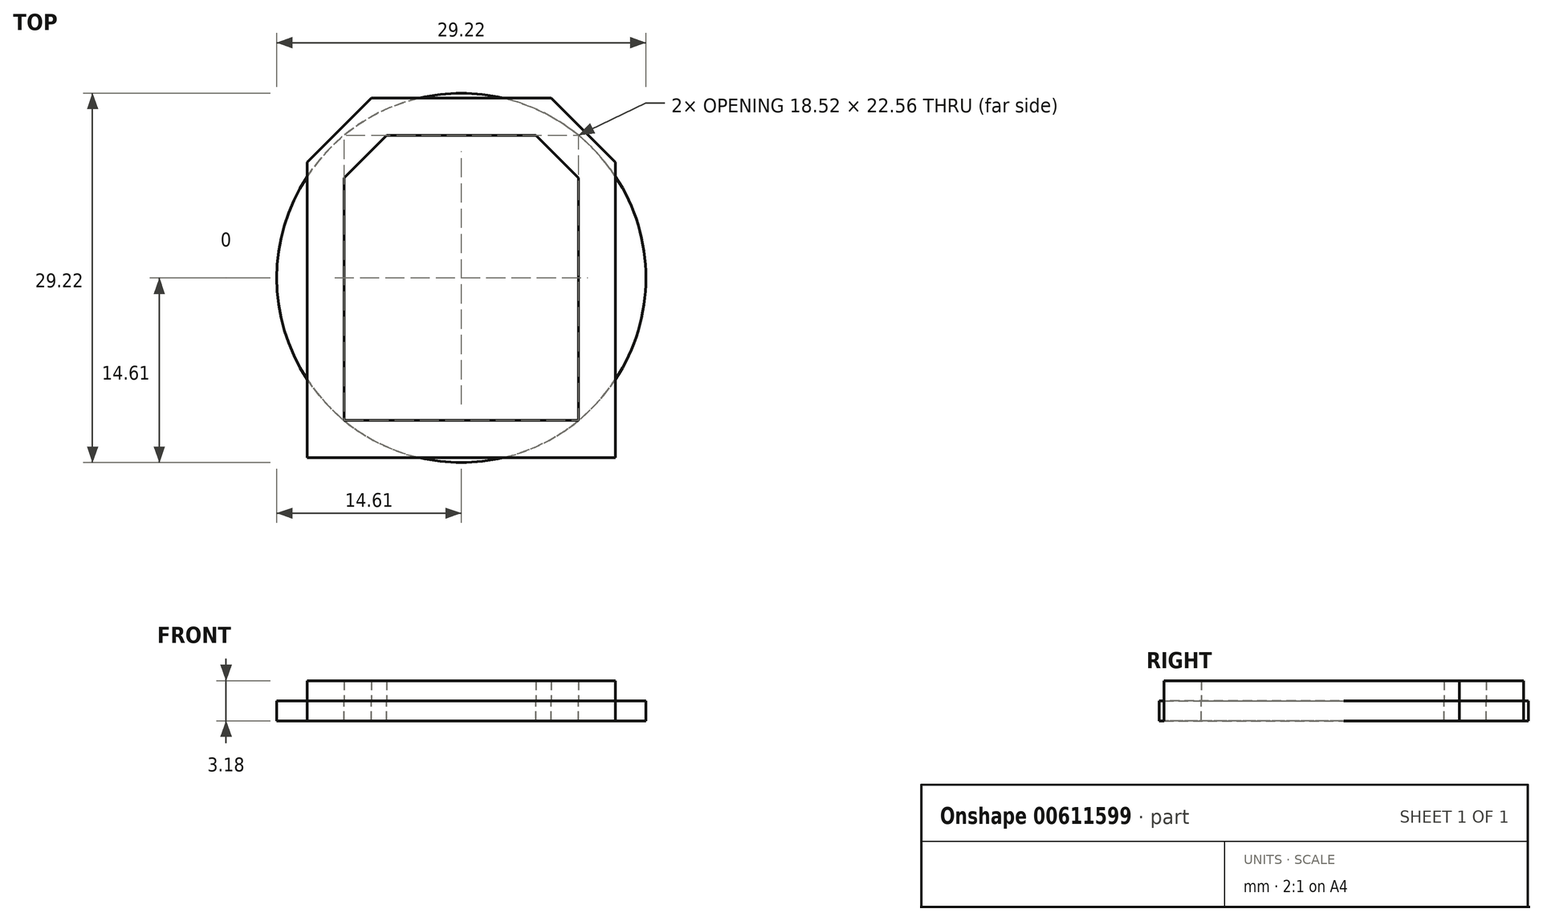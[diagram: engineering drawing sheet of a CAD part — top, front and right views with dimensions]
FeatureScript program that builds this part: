
annotation { "Feature Type Name" : "Feature", "Feature Type Description" : "" }
export const myFeature = defineFeature(function(context is Context, id is Id, definition is map)
    precondition{}
    {
        {
            var Q0;
            Q0=qCreatedBy(makeId("Top.planeOp"),FACE);
            var sketch = newSketch(context, id + "F0", { "sketchPlane" : qUnion([Q0])});
            skLineSegment(sketch, "E0.bottom", {"start": v(12.2, -14.22) * mm, "end": v(-12.2, -14.22) * mm});
            skLineSegment(sketch, "E0.top", {"start": v(7.12, 14.22) * mm, "end": v(-7.12, 14.22) * mm});
            skLineSegment(sketch, "E0.left", {"start": v(12.2, -14.22) * mm, "end": v(12.2, 9.14) * mm});
            skLineSegment(sketch, "E0.right", {"start": v(-12.2, -14.22) * mm, "end": v(-12.2, 9.14) * mm});
            skPoint(sketch, "E0.middle", {"position": v(0, 0) * mm});
            skLineSegment(sketch, "E1", {"start": v(12.2, 9.14) * mm, "end": v(7.12, 14.22) * mm});
            skLineSegment(sketch, "E2.MirrorCS", {"start": v(-12.2, 9.14) * mm, "end": v(-7.12, 14.22) * mm});
            skPoint(sketch, "E3.orphan", {"position": v(-12.2, 14.22) * mm});
            skPoint(sketch, "E4.orphan", {"position": v(12.2, 14.22) * mm});
            skLineSegment(sketch, "E5.0", {"start": v(-9.26, -11.28) * mm, "end": v(-9.26, 7.92) * mm});
            skLineSegment(sketch, "E5.1", {"start": v(5.9, 11.28) * mm, "end": v(-5.9, 11.28) * mm});
            skLineSegment(sketch, "E5.2", {"start": v(9.26, 7.92) * mm, "end": v(5.9, 11.28) * mm});
            skLineSegment(sketch, "E5.3", {"start": v(-9.26, 7.92) * mm, "end": v(-5.9, 11.28) * mm});
            skLineSegment(sketch, "E5.4", {"start": v(9.26, -11.28) * mm, "end": v(9.26, 7.92) * mm});
            skLineSegment(sketch, "E5.5", {"start": v(9.26, -11.28) * mm, "end": v(-9.26, -11.28) * mm});
            skSolve(sketch);
        }
        {
            var Q0;
            Q0=makeQuery(id+"F0.imprint","IMPRINT",FACE,{"disambiguationData":[TD([[makeQuery(id+"F0.imprint","IMPRINT",EDGE,{"derivedFrom":sQuery(id+"F0.wireOp",EDGE,"E0.bottom")}),-1.0]])]});
            extrude(context, id + "F1", {"entities" : qUnion([Q0]), "depth" : 1.59 * mm, "offsetDistance" : 25.4 * mm});
        }
        {
            var Q0;
            Q0=qCreatedBy(makeId("Top.planeOp"),FACE);
            var sketch = newSketch(context, id + "F2", { "sketchPlane" : qUnion([Q0])});
            skCircle(sketch, "E6", {"center": v(0, 0) * mm, "radius": 14.6 * mm});
            skSolve(sketch);
        }
        {
            var Q0;
            Q0=makeQuery(id+"F2.imprint","IMPRINT",FACE,{"disambiguationData":[TD([[makeQuery(id+"F2.imprint","IMPRINT",EDGE,{"derivedFrom":sQuery(id+"F2.wireOp",EDGE,"E6")}),1.0]])]});
            var Q1;
            Q1=sQuery(id+"F2.wireOp",EDGE,"E6");
            extrude(context, id + "F3", {"entities" : qUnion([Q0]), "surfaceEntities" : qUnion([Q1]), "oppositeDirection" : true, "depth" : 1.59 * mm, "offsetDistance" : 25.4 * mm});
        }
        {
            var Q0;
            Q0=makeQuery(id+"F1.opExtrude","CAP_FACE",FACE,{"disambiguationData":[OSD([sQuery(id+"F0.wireOp",EDGE,"E0.bottom"),sQuery(id+"F0.wireOp",EDGE,"E0.top"),sQuery(id+"F0.wireOp",EDGE,"E0.left"),sQuery(id+"F0.wireOp",EDGE,"E0.right"),sQuery(id+"F0.wireOp",EDGE,"E1"),sQuery(id+"F0.wireOp",EDGE,"E2.MirrorCS"),sQuery(id+"F0.wireOp",EDGE,"E5.0"),sQuery(id+"F0.wireOp",EDGE,"E5.1"),sQuery(id+"F0.wireOp",EDGE,"E5.2"),sQuery(id+"F0.wireOp",EDGE,"E5.3"),sQuery(id+"F0.wireOp",EDGE,"E5.4"),sQuery(id+"F0.wireOp",EDGE,"E5.5")])],"isStart":true});
            var Q1;
            Q1=makeQuery(id+"F3.opExtrude","CAP_FACE",FACE,{"disambiguationData":[OSD([sQuery(id+"F2.wireOp",EDGE,"E6")])],"isStart":false});
            extrude(context, id + "F4", {"entities" : qUnion([Q0]), "endBound" : BoundingType.UP_TO_SURFACE, "depth" : 25.4 * mm, "endBoundEntityFace" : qUnion([Q1]), "offsetDistance" : 25.4 * mm});
        }
    });
